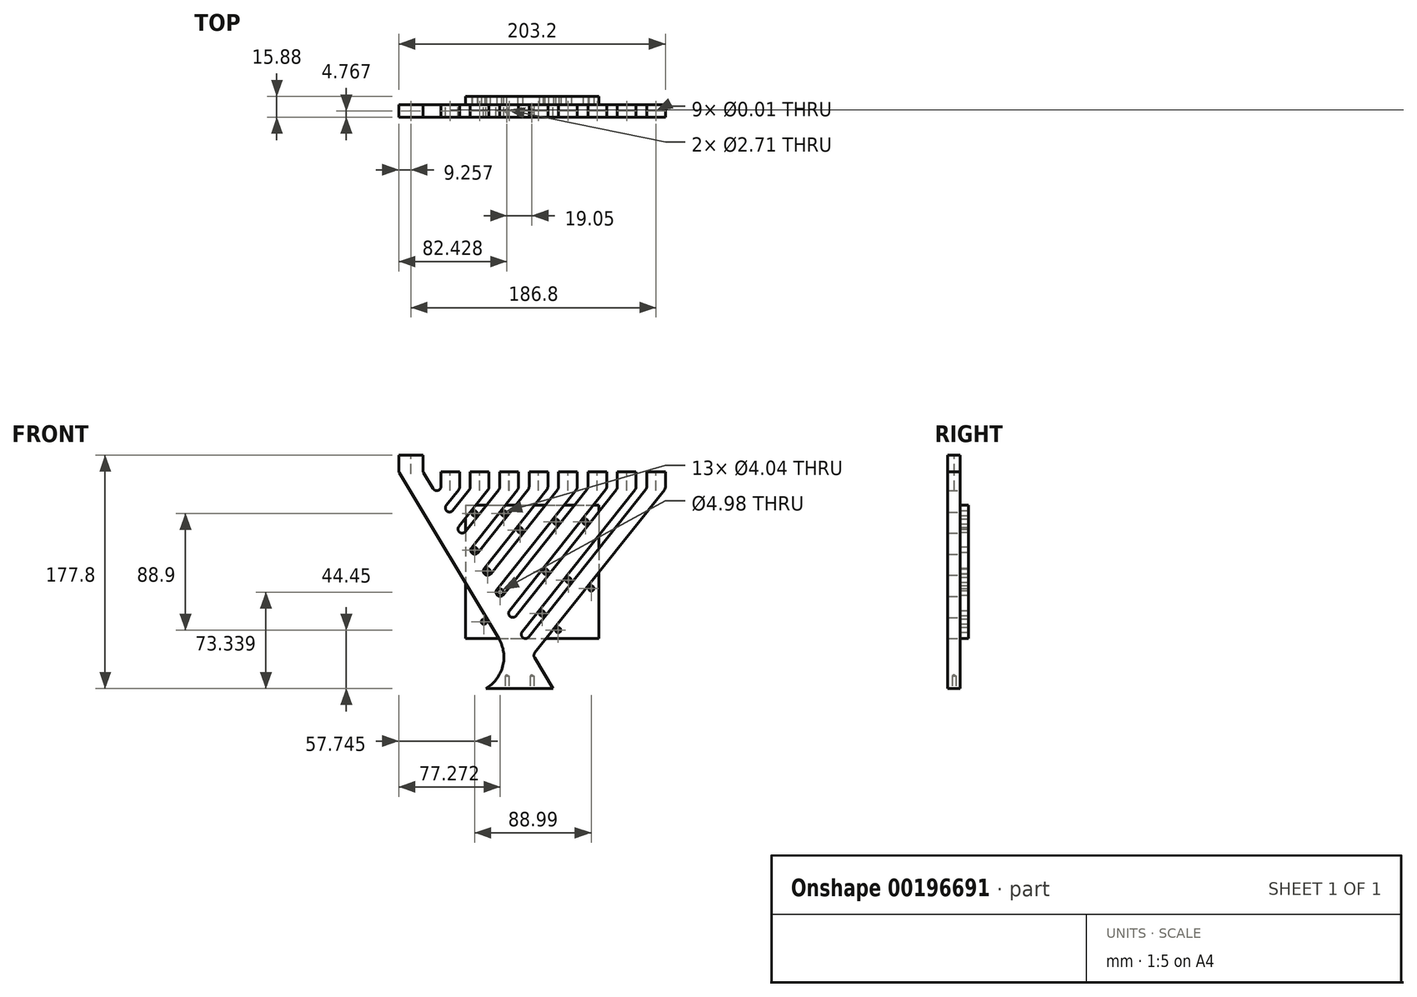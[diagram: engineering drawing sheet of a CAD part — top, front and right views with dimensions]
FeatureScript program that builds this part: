
annotation { "Feature Type Name" : "Feature", "Feature Type Description" : "" }
export const myFeature = defineFeature(function(context is Context, id is Id, definition is map)
    precondition{}
    {
        {
            var Q0;
            Q0=qCreatedBy(makeId("Front.planeOp"),FACE);
            var sketch = newSketch(context, id + "F0", { "sketchPlane" : qUnion([Q0])});
            skLineSegment(sketch, "E0", {"start": v(0, -12.7) * mm, "end": v(76.2, -139.7) * mm});
            skLineSegment(sketch, "E1", {"start": v(66.33, -177.8) * mm, "end": v(117.57, -177.8) * mm});
            skLineSegment(sketch, "E2", {"start": v(117.57, -177.8) * mm, "end": v(102.33, -152.4) * mm});
            skLineSegment(sketch, "E3", {"start": v(102.33, -152.4) * mm, "end": v(203.2, -25.4) * mm});
            skArc(sketch, "E4", {"start": v(76.2, -139.7) * mm, "mid": v(79.25, -160.82) * mm, "end": v(66.33, -177.8) * mm});
            skLineSegment(sketch, "E5.1.0.0", {"start": v(92.7, -136.34) * mm, "end": v(193.56, -9.34) * mm});
            skLineSegment(sketch, "E5.2.0.0", {"start": v(83.06, -120.27) * mm, "end": v(183.92, 6.73) * mm});
            skLineSegment(sketch, "E5.direction1", {"start": v(102.33, -152.4) * mm, "end": v(92.7, -136.34) * mm, "construction": true});
            skLineSegment(sketch, "E6.0.3.0", {"start": v(73.42, -104.2) * mm, "end": v(174.29, 22.8) * mm});
            skLineSegment(sketch, "E6.0.4.0", {"start": v(63.78, -88.14) * mm, "end": v(164.65, 38.86) * mm});
            skLineSegment(sketch, "E6.0.5.0", {"start": v(54.14, -72.08) * mm, "end": v(155, 54.92) * mm});
            skLineSegment(sketch, "E6.0.6.0", {"start": v(44.5, -56.02) * mm, "end": v(145.37, 70.98) * mm});
            skLineSegment(sketch, "E6.0.7.0", {"start": v(34.87, -39.95) * mm, "end": v(135.73, 87.05) * mm});
            skLineSegment(sketch, "E7", {"start": v(96.18, -142.15) * mm, "end": v(197.05, -15.15) * mm});
            skLineSegment(sketch, "E8.1.0.0", {"start": v(86.55, -126.09) * mm, "end": v(187.41, 0.91) * mm});
            skLineSegment(sketch, "E8.2.0.0", {"start": v(76.9, -110.02) * mm, "end": v(177.77, 16.98) * mm});
            skLineSegment(sketch, "E8.direction1", {"start": v(96.18, -142.15) * mm, "end": v(86.55, -126.09) * mm, "construction": true});
            skLineSegment(sketch, "E9.0.3.0", {"start": v(67.27, -93.96) * mm, "end": v(168.14, 33.04) * mm});
            skLineSegment(sketch, "E9.0.4.0", {"start": v(57.63, -77.9) * mm, "end": v(158.5, 49.1) * mm});
            skLineSegment(sketch, "E9.0.5.0", {"start": v(48, -61.83) * mm, "end": v(148.86, 65.17) * mm});
            skLineSegment(sketch, "E9.0.6.0", {"start": v(38.35, -45.77) * mm, "end": v(139.22, 81.23) * mm});
            skLineSegment(sketch, "E9.0.7.0", {"start": v(28.72, -29.7) * mm, "end": v(129.58, 97.3) * mm});
            skLineSegment(sketch, "E10", {"start": v(203.2, -25.4) * mm, "end": v(-58.22, -25.4) * mm});
            skLineSegment(sketch, "E11", {"start": v(102.33, -152.4) * mm, "end": v(28.72, -29.7) * mm});
            skLineSegment(sketch, "E12", {"start": v(28.72, -29.7) * mm, "end": v(18.51, -12.7) * mm});
            skLineSegment(sketch, "E13", {"start": v(18.51, -12.7) * mm, "end": v(0, -12.7) * mm});
            skPoint(sketch, "E14", {"position": v(180.8, -25.4) * mm});
            skLineSegment(sketch, "E15", {"start": v(66.33, -177.8) * mm, "end": v(34.1, -196.4) * mm, "construction": true});
            skLineSegment(sketch, "E16", {"start": v(0, -12.7) * mm, "end": v(0, 0) * mm});
            skLineSegment(sketch, "E17", {"start": v(18.51, -12.7) * mm, "end": v(203.2, -12.7) * mm, "construction": true});
            skPoint(sketch, "E18", {"position": v(32.14, -25.4) * mm});
            skPoint(sketch, "E19", {"position": v(46.42, -25.4) * mm});
            skPoint(sketch, "E20", {"position": v(54.53, -25.4) * mm});
            skPoint(sketch, "E21", {"position": v(68.82, -25.4) * mm});
            skPoint(sketch, "E22", {"position": v(76.93, -25.4) * mm});
            skPoint(sketch, "E23", {"position": v(91.22, -25.4) * mm});
            skPoint(sketch, "E24", {"position": v(99.33, -25.4) * mm});
            skPoint(sketch, "E25", {"position": v(114.21, -24.64) * mm});
            skPoint(sketch, "E26", {"position": v(121.72, -25.4) * mm});
            skPoint(sketch, "E27", {"position": v(136.01, -25.4) * mm});
            skPoint(sketch, "E28", {"position": v(144.12, -25.4) * mm});
            skPoint(sketch, "E29", {"position": v(158.4, -25.4) * mm});
            skPoint(sketch, "E30", {"position": v(166.52, -25.4) * mm});
            skPoint(sketch, "E31", {"position": v(188.91, -25.4) * mm});
            skLineSegment(sketch, "E32", {"start": v(117.57, -177.8) * mm, "end": v(125.2, -190.5) * mm});
            skSolve(sketch);
        }
        {
            var Q0;
            Q0=makeQuery(id+"F0.imprint","IMPRINT",FACE,{"disambiguationData":[TD([[makeQuery(id+"F0.imprint","IMPRINT",EDGE,{"derivedFrom":sQuery(id+"F0.wireOp",EDGE,"E1")}),1.0]])]});
            var Q1;
            {var subQ0=sQuery(id+"F0.wireOp",EDGE,"E13");Q1=makeQuery(id+"F0.imprint","IMPRINT",FACE,{"disambiguationData":[TD([[makeQuery(id+"F0.imprint","IMPRINT",EDGE,{"derivedFrom":subQ0}),1.0]])]});}
            var Q2;
            {var subQ0=sQuery(id+"F0.wireOp",EDGE,"E11");var subQ1=sQuery(id+"F0.wireOp",EDGE,"E6.0.7.0");var subQ2=makeQuery(id+"F0.imprint","INTERSECT",VERTEX,{"derivedFrom":[subQ1,subQ0]});Q2=makeQuery(id+"F0.imprint","IMPRINT",FACE,{"disambiguationData":[TD([[makeQuery(id+"F0.imprint","IMPRINT",EDGE,{"disambiguationData":[TD([[subQ2,-1.0]])],"derivedFrom":subQ1}),1.0]])]});}
            var Q3;
            {var subQ0=sQuery(id+"F0.wireOp",EDGE,"E11");var subQ1=sQuery(id+"F0.wireOp",EDGE,"E6.0.6.0");var subQ2=makeQuery(id+"F0.imprint","INTERSECT",VERTEX,{"derivedFrom":[subQ1,subQ0]});Q3=makeQuery(id+"F0.imprint","IMPRINT",FACE,{"disambiguationData":[TD([[makeQuery(id+"F0.imprint","IMPRINT",EDGE,{"disambiguationData":[TD([[subQ2,-1.0]])],"derivedFrom":subQ1}),1.0]])]});}
            var Q4;
            {var subQ0=sQuery(id+"F0.wireOp",EDGE,"E11");var subQ1=sQuery(id+"F0.wireOp",EDGE,"E6.0.5.0");var subQ2=makeQuery(id+"F0.imprint","INTERSECT",VERTEX,{"derivedFrom":[subQ1,subQ0]});Q4=makeQuery(id+"F0.imprint","IMPRINT",FACE,{"disambiguationData":[TD([[makeQuery(id+"F0.imprint","IMPRINT",EDGE,{"disambiguationData":[TD([[subQ2,-1.0]])],"derivedFrom":subQ1}),1.0]])]});}
            var Q5;
            {var subQ0=sQuery(id+"F0.wireOp",EDGE,"E11");var subQ1=sQuery(id+"F0.wireOp",EDGE,"E6.0.4.0");var subQ2=makeQuery(id+"F0.imprint","INTERSECT",VERTEX,{"derivedFrom":[subQ1,subQ0]});Q5=makeQuery(id+"F0.imprint","IMPRINT",FACE,{"disambiguationData":[TD([[makeQuery(id+"F0.imprint","IMPRINT",EDGE,{"disambiguationData":[TD([[subQ2,-1.0]])],"derivedFrom":subQ1}),1.0]])]});}
            var Q6;
            {var subQ0=sQuery(id+"F0.wireOp",EDGE,"E11");var subQ1=sQuery(id+"F0.wireOp",EDGE,"E6.0.3.0");var subQ2=makeQuery(id+"F0.imprint","INTERSECT",VERTEX,{"derivedFrom":[subQ1,subQ0]});Q6=makeQuery(id+"F0.imprint","IMPRINT",FACE,{"disambiguationData":[TD([[makeQuery(id+"F0.imprint","IMPRINT",EDGE,{"disambiguationData":[TD([[subQ2,-1.0]])],"derivedFrom":subQ1}),1.0]])]});}
            var Q7;
            {var subQ0=sQuery(id+"F0.wireOp",EDGE,"E11");var subQ1=sQuery(id+"F0.wireOp",EDGE,"E5.2.0.0");var subQ2=makeQuery(id+"F0.imprint","INTERSECT",VERTEX,{"derivedFrom":[subQ1,subQ0]});Q7=makeQuery(id+"F0.imprint","IMPRINT",FACE,{"disambiguationData":[TD([[makeQuery(id+"F0.imprint","IMPRINT",EDGE,{"disambiguationData":[TD([[subQ2,-1.0]])],"derivedFrom":subQ1}),1.0]])]});}
            var Q8;
            {var subQ0=sQuery(id+"F0.wireOp",EDGE,"E11");var subQ1=sQuery(id+"F0.wireOp",EDGE,"E5.1.0.0");var subQ2=makeQuery(id+"F0.imprint","INTERSECT",VERTEX,{"derivedFrom":[subQ1,subQ0]});Q8=makeQuery(id+"F0.imprint","IMPRINT",FACE,{"disambiguationData":[TD([[makeQuery(id+"F0.imprint","IMPRINT",EDGE,{"disambiguationData":[TD([[subQ2,-1.0]])],"derivedFrom":subQ1}),1.0]])]});}
            var Q9;
            {var subQ0=sQuery(id+"F0.wireOp",EDGE,"E3");Q9=makeQuery(id+"F0.imprint","IMPRINT",FACE,{"disambiguationData":[TD([[makeQuery(id+"F0.imprint","IMPRINT",EDGE,{"derivedFrom":subQ0}),1.0]])]});}
            extrude(context, id + "F1", {"entities" : qUnion([Q0, Q1, Q2, Q3, Q4, Q5, Q6, Q7, Q8, Q9]), "flatOperationType" : FlatOperationType.REMOVE, "offsetDistance" : 25.4 * mm, "depth" : 9.52 * mm, "domain" : OperationDomain.MODEL});
        }
        {
            var Q0;
            Q0=makeQuery(id+"F1.opExtrude","SWEPT_EDGE",EDGE,{"disambiguationData":[OSD([sQuery(id+"F0.wireOp",EDGE,"E9.0.6.0"),sQuery(id+"F0.wireOp",EDGE,"E11")])]});
            var Q1;
            Q1=makeQuery(id+"F1.opExtrude","SWEPT_EDGE",EDGE,{"disambiguationData":[OSD([sQuery(id+"F0.wireOp",EDGE,"E9.0.5.0"),sQuery(id+"F0.wireOp",EDGE,"E11")])]});
            var Q2;
            Q2=makeQuery(id+"F1.opExtrude","SWEPT_EDGE",EDGE,{"disambiguationData":[OSD([sQuery(id+"F0.wireOp",EDGE,"E9.0.4.0"),sQuery(id+"F0.wireOp",EDGE,"E11")])]});
            var Q3;
            Q3=makeQuery(id+"F1.opExtrude","SWEPT_EDGE",EDGE,{"disambiguationData":[OSD([sQuery(id+"F0.wireOp",EDGE,"E9.0.3.0"),sQuery(id+"F0.wireOp",EDGE,"E11")])]});
            var Q4;
            Q4=makeQuery(id+"F1.opExtrude","SWEPT_EDGE",EDGE,{"disambiguationData":[OSD([sQuery(id+"F0.wireOp",EDGE,"E8.2.0.0"),sQuery(id+"F0.wireOp",EDGE,"E11")])]});
            var Q5;
            Q5=makeQuery(id+"F1.opExtrude","SWEPT_EDGE",EDGE,{"disambiguationData":[OSD([sQuery(id+"F0.wireOp",EDGE,"E8.1.0.0"),sQuery(id+"F0.wireOp",EDGE,"E11")])]});
            var Q6;
            Q6=makeQuery(id+"F1.opExtrude","SWEPT_EDGE",EDGE,{"disambiguationData":[OSD([sQuery(id+"F0.wireOp",EDGE,"E7"),sQuery(id+"F0.wireOp",EDGE,"E11")])]});
            fillet(context, id + "F2", {"entities" : qUnion([Q0, Q1, Q2, Q3, Q4, Q5, Q6]), "radius" : 3.17 * mm, "tangentPropagation" : true, "allowEdgeOverflow" : false});
        }
        {
            var Q0;
            Q0=makeQuery(id+"F1.opExtrude","SWEPT_EDGE",EDGE,{"disambiguationData":[OSD([sQuery(id+"F0.wireOp",EDGE,"E6.0.7.0"),sQuery(id+"F0.wireOp",EDGE,"E11")])]});
            var Q1;
            Q1=makeQuery(id+"F1.opExtrude","SWEPT_EDGE",EDGE,{"disambiguationData":[OSD([sQuery(id+"F0.wireOp",EDGE,"E6.0.6.0"),sQuery(id+"F0.wireOp",EDGE,"E11")])]});
            var Q2;
            Q2=makeQuery(id+"F1.opExtrude","SWEPT_EDGE",EDGE,{"disambiguationData":[OSD([sQuery(id+"F0.wireOp",EDGE,"E6.0.5.0"),sQuery(id+"F0.wireOp",EDGE,"E11")])]});
            var Q3;
            Q3=makeQuery(id+"F1.opExtrude","SWEPT_EDGE",EDGE,{"disambiguationData":[OSD([sQuery(id+"F0.wireOp",EDGE,"E6.0.4.0"),sQuery(id+"F0.wireOp",EDGE,"E11")])]});
            var Q4;
            Q4=makeQuery(id+"F1.opExtrude","SWEPT_EDGE",EDGE,{"disambiguationData":[OSD([sQuery(id+"F0.wireOp",EDGE,"E6.0.3.0"),sQuery(id+"F0.wireOp",EDGE,"E11")])]});
            var Q5;
            Q5=makeQuery(id+"F1.opExtrude","SWEPT_EDGE",EDGE,{"disambiguationData":[OSD([sQuery(id+"F0.wireOp",EDGE,"E5.2.0.0"),sQuery(id+"F0.wireOp",EDGE,"E11")])]});
            var Q6;
            Q6=makeQuery(id+"F1.opExtrude","SWEPT_EDGE",EDGE,{"disambiguationData":[OSD([sQuery(id+"F0.wireOp",EDGE,"E5.1.0.0"),sQuery(id+"F0.wireOp",EDGE,"E11")])]});
            var Q7;
            Q7=makeQuery(id+"F1.opExtrude","SWEPT_EDGE",EDGE,{"disambiguationData":[OSD([sQuery(id+"F0.wireOp",EDGE,"E2"),sQuery(id+"F0.wireOp",EDGE,"E3"),sQuery(id+"F0.wireOp",EDGE,"E11")])]});
            fillet(context, id + "F3", {"entities" : qUnion([Q0, Q1, Q2, Q3, Q4, Q5, Q6, Q7]), "radius" : 3.17 * mm, "tangentPropagation" : true, "allowEdgeOverflow" : false});
        }
        {
            var Q0;
            Q0=makeQuery(id+"F1.opExtrude","SWEPT_FACE",FACE,{"disambiguationData":[OSD([sQuery(id+"F0.wireOp",EDGE,"E13")])]});
            extrude(context, id + "F4", {"entities" : qUnion([Q0]), "operationType" : NewBodyOperationType.ADD, "depth" : 12.7 * mm});
        }
        {
            var Q0;
            {var subQ0=sQuery(id+"F0.wireOp",EDGE,"E10");Q0=makeQuery(id+"F1.opExtrude","SWEPT_FACE",FACE,{"disambiguationData":[OSD([subQ0]),TDD([makeQuery(id+"F0.imprint","IMPRINT",EDGE,{"disambiguationData":[TD([[makeQuery(id+"F0.imprint","INTERSECT",VERTEX,{"derivedFrom":[sQuery(id+"F0.wireOp",EDGE,"E6.0.7.0"),subQ0]}),-1.0]])],"derivedFrom":subQ0})])]});}
            var Q1;
            {var subQ0=sQuery(id+"F0.wireOp",EDGE,"E10");Q1=makeQuery(id+"F1.opExtrude","SWEPT_FACE",FACE,{"disambiguationData":[OSD([subQ0]),TDD([makeQuery(id+"F0.imprint","IMPRINT",EDGE,{"disambiguationData":[TD([[makeQuery(id+"F0.imprint","INTERSECT",VERTEX,{"derivedFrom":[sQuery(id+"F0.wireOp",EDGE,"E6.0.6.0"),subQ0]}),-1.0]])],"derivedFrom":subQ0})])]});}
            var Q2;
            {var subQ0=sQuery(id+"F0.wireOp",EDGE,"E10");Q2=makeQuery(id+"F1.opExtrude","SWEPT_FACE",FACE,{"disambiguationData":[OSD([subQ0]),TDD([makeQuery(id+"F0.imprint","IMPRINT",EDGE,{"disambiguationData":[TD([[makeQuery(id+"F0.imprint","INTERSECT",VERTEX,{"derivedFrom":[sQuery(id+"F0.wireOp",EDGE,"E6.0.5.0"),subQ0]}),-1.0]])],"derivedFrom":subQ0})])]});}
            var Q3;
            {var subQ0=sQuery(id+"F0.wireOp",EDGE,"E10");Q3=makeQuery(id+"F1.opExtrude","SWEPT_FACE",FACE,{"disambiguationData":[OSD([subQ0]),TDD([makeQuery(id+"F0.imprint","IMPRINT",EDGE,{"disambiguationData":[TD([[makeQuery(id+"F0.imprint","INTERSECT",VERTEX,{"derivedFrom":[sQuery(id+"F0.wireOp",EDGE,"E6.0.4.0"),subQ0]}),-1.0]])],"derivedFrom":subQ0})])]});}
            var Q4;
            {var subQ0=sQuery(id+"F0.wireOp",EDGE,"E10");Q4=makeQuery(id+"F1.opExtrude","SWEPT_FACE",FACE,{"disambiguationData":[OSD([subQ0]),TDD([makeQuery(id+"F0.imprint","IMPRINT",EDGE,{"disambiguationData":[TD([[makeQuery(id+"F0.imprint","INTERSECT",VERTEX,{"derivedFrom":[sQuery(id+"F0.wireOp",EDGE,"E6.0.3.0"),subQ0]}),-1.0]])],"derivedFrom":subQ0})])]});}
            var Q5;
            {var subQ0=sQuery(id+"F0.wireOp",EDGE,"E10");Q5=makeQuery(id+"F1.opExtrude","SWEPT_FACE",FACE,{"disambiguationData":[OSD([subQ0]),TDD([makeQuery(id+"F0.imprint","IMPRINT",EDGE,{"disambiguationData":[TD([[makeQuery(id+"F0.imprint","INTERSECT",VERTEX,{"derivedFrom":[sQuery(id+"F0.wireOp",EDGE,"E5.2.0.0"),subQ0]}),-1.0]])],"derivedFrom":subQ0})])]});}
            var Q6;
            {var subQ0=sQuery(id+"F0.wireOp",EDGE,"E10");Q6=makeQuery(id+"F1.opExtrude","SWEPT_FACE",FACE,{"disambiguationData":[OSD([subQ0]),TDD([makeQuery(id+"F0.imprint","IMPRINT",EDGE,{"disambiguationData":[TD([[makeQuery(id+"F0.imprint","INTERSECT",VERTEX,{"derivedFrom":[sQuery(id+"F0.wireOp",EDGE,"E5.1.0.0"),subQ0]}),-1.0]])],"derivedFrom":subQ0})])]});}
            var Q7;
            {var subQ0=sQuery(id+"F0.wireOp",EDGE,"E10");Q7=makeQuery(id+"F1.opExtrude","SWEPT_FACE",FACE,{"disambiguationData":[OSD([subQ0]),TDD([makeQuery(id+"F0.imprint","IMPRINT",EDGE,{"disambiguationData":[TD([[makeQuery(id+"F0.imprint","INTERSECT",VERTEX,{"derivedFrom":[sQuery(id+"F0.wireOp",EDGE,"E3"),subQ0]}),-1.0]])],"derivedFrom":subQ0})])]});}
            extrude(context, id + "F5", {"entities" : qUnion([Q0, Q1, Q2, Q3, Q4, Q5, Q6, Q7]), "operationType" : NewBodyOperationType.ADD, "depth" : 12.7 * mm});
        }
        {
            var Q0;
            {var subQ0=sQuery(id+"F0.wireOp",EDGE,"E10");var subQ1=sQuery(id+"F0.wireOp",EDGE,"E9.0.6.0");Q0=makeQuery(id+"F5.boolean.opBoolean","MERGE",EDGE,{"derivedFrom":[makeQuery(id+"F1.opExtrude","SWEPT_EDGE",EDGE,{"disambiguationData":[OSD([subQ1,subQ0])]}),makeQuery(id+"F5.opExtrude","CAP_EDGE",EDGE,{"disambiguationData":[OSD([subQ1,subQ0])],"isStart":true})]});}
            var Q1;
            {var subQ0=sQuery(id+"F0.wireOp",EDGE,"E10");var subQ1=sQuery(id+"F0.wireOp",EDGE,"E9.0.5.0");Q1=makeQuery(id+"F5.boolean.opBoolean","MERGE",EDGE,{"derivedFrom":[makeQuery(id+"F1.opExtrude","SWEPT_EDGE",EDGE,{"disambiguationData":[OSD([subQ1,subQ0])]}),makeQuery(id+"F5.opExtrude","CAP_EDGE",EDGE,{"disambiguationData":[OSD([subQ1,subQ0])],"isStart":true})]});}
            var Q2;
            {var subQ0=sQuery(id+"F0.wireOp",EDGE,"E10");var subQ1=sQuery(id+"F0.wireOp",EDGE,"E9.0.4.0");Q2=makeQuery(id+"F5.boolean.opBoolean","MERGE",EDGE,{"derivedFrom":[makeQuery(id+"F1.opExtrude","SWEPT_EDGE",EDGE,{"disambiguationData":[OSD([subQ1,subQ0])]}),makeQuery(id+"F5.opExtrude","CAP_EDGE",EDGE,{"disambiguationData":[OSD([subQ1,subQ0])],"isStart":true})]});}
            var Q3;
            {var subQ0=sQuery(id+"F0.wireOp",EDGE,"E10");var subQ1=sQuery(id+"F0.wireOp",EDGE,"E9.0.3.0");Q3=makeQuery(id+"F5.boolean.opBoolean","MERGE",EDGE,{"derivedFrom":[makeQuery(id+"F1.opExtrude","SWEPT_EDGE",EDGE,{"disambiguationData":[OSD([subQ1,subQ0])]}),makeQuery(id+"F5.opExtrude","CAP_EDGE",EDGE,{"disambiguationData":[OSD([subQ1,subQ0])],"isStart":true})]});}
            var Q4;
            {var subQ0=sQuery(id+"F0.wireOp",EDGE,"E10");var subQ1=sQuery(id+"F0.wireOp",EDGE,"E8.2.0.0");Q4=makeQuery(id+"F5.boolean.opBoolean","MERGE",EDGE,{"derivedFrom":[makeQuery(id+"F1.opExtrude","SWEPT_EDGE",EDGE,{"disambiguationData":[OSD([subQ1,subQ0])]}),makeQuery(id+"F5.opExtrude","CAP_EDGE",EDGE,{"disambiguationData":[OSD([subQ1,subQ0])],"isStart":true})]});}
            var Q5;
            {var subQ0=sQuery(id+"F0.wireOp",EDGE,"E10");var subQ1=sQuery(id+"F0.wireOp",EDGE,"E8.1.0.0");Q5=makeQuery(id+"F5.boolean.opBoolean","MERGE",EDGE,{"derivedFrom":[makeQuery(id+"F1.opExtrude","SWEPT_EDGE",EDGE,{"disambiguationData":[OSD([subQ1,subQ0])]}),makeQuery(id+"F5.opExtrude","CAP_EDGE",EDGE,{"disambiguationData":[OSD([subQ1,subQ0])],"isStart":true})]});}
            var Q6;
            {var subQ0=sQuery(id+"F0.wireOp",EDGE,"E10");var subQ1=sQuery(id+"F0.wireOp",EDGE,"E7");Q6=makeQuery(id+"F5.boolean.opBoolean","MERGE",EDGE,{"derivedFrom":[makeQuery(id+"F1.opExtrude","SWEPT_EDGE",EDGE,{"disambiguationData":[OSD([subQ1,subQ0])]}),makeQuery(id+"F5.opExtrude","CAP_EDGE",EDGE,{"disambiguationData":[OSD([subQ1,subQ0])],"isStart":true})]});}
            var Q7;
            {var subQ0=sQuery(id+"F0.wireOp",EDGE,"E13");var subQ1=sQuery(id+"F0.wireOp",EDGE,"E12");Q7=makeQuery(id+"F4.boolean.opBoolean","MERGE",EDGE,{"derivedFrom":[makeQuery(id+"F1.opExtrude","SWEPT_EDGE",EDGE,{"disambiguationData":[OSD([subQ1,subQ0])]}),makeQuery(id+"F4.opExtrude","CAP_EDGE",EDGE,{"disambiguationData":[OSD([subQ1,subQ0])],"isStart":true})]});}
            fillet(context, id + "F6", {"entities" : qUnion([Q0, Q1, Q2, Q3, Q4, Q5, Q6, Q7]), "radius" : 3.17 * mm, "tangentPropagation" : true, "allowEdgeOverflow" : false});
        }
        {
            var Q0;
            {var subQ0=sQuery(id+"F0.wireOp",EDGE,"E10");var subQ1=sQuery(id+"F0.wireOp",EDGE,"E6.0.7.0");Q0=makeQuery(id+"F5.boolean.opBoolean","MERGE",EDGE,{"derivedFrom":[makeQuery(id+"F1.opExtrude","SWEPT_EDGE",EDGE,{"disambiguationData":[OSD([subQ1,subQ0])]}),makeQuery(id+"F5.opExtrude","CAP_EDGE",EDGE,{"disambiguationData":[OSD([subQ1,subQ0])],"isStart":true})]});}
            var Q1;
            {var subQ0=sQuery(id+"F0.wireOp",EDGE,"E10");var subQ1=sQuery(id+"F0.wireOp",EDGE,"E6.0.6.0");Q1=makeQuery(id+"F5.boolean.opBoolean","MERGE",EDGE,{"derivedFrom":[makeQuery(id+"F1.opExtrude","SWEPT_EDGE",EDGE,{"disambiguationData":[OSD([subQ1,subQ0])]}),makeQuery(id+"F5.opExtrude","CAP_EDGE",EDGE,{"disambiguationData":[OSD([subQ1,subQ0])],"isStart":true})]});}
            var Q2;
            {var subQ0=sQuery(id+"F0.wireOp",EDGE,"E10");var subQ1=sQuery(id+"F0.wireOp",EDGE,"E6.0.5.0");Q2=makeQuery(id+"F5.boolean.opBoolean","MERGE",EDGE,{"derivedFrom":[makeQuery(id+"F1.opExtrude","SWEPT_EDGE",EDGE,{"disambiguationData":[OSD([subQ1,subQ0])]}),makeQuery(id+"F5.opExtrude","CAP_EDGE",EDGE,{"disambiguationData":[OSD([subQ1,subQ0])],"isStart":true})]});}
            var Q3;
            {var subQ0=sQuery(id+"F0.wireOp",EDGE,"E10");var subQ1=sQuery(id+"F0.wireOp",EDGE,"E6.0.4.0");Q3=makeQuery(id+"F5.boolean.opBoolean","MERGE",EDGE,{"derivedFrom":[makeQuery(id+"F1.opExtrude","SWEPT_EDGE",EDGE,{"disambiguationData":[OSD([subQ1,subQ0])]}),makeQuery(id+"F5.opExtrude","CAP_EDGE",EDGE,{"disambiguationData":[OSD([subQ1,subQ0])],"isStart":true})]});}
            var Q4;
            {var subQ0=sQuery(id+"F0.wireOp",EDGE,"E10");var subQ1=sQuery(id+"F0.wireOp",EDGE,"E6.0.3.0");Q4=makeQuery(id+"F5.boolean.opBoolean","MERGE",EDGE,{"derivedFrom":[makeQuery(id+"F1.opExtrude","SWEPT_EDGE",EDGE,{"disambiguationData":[OSD([subQ1,subQ0])]}),makeQuery(id+"F5.opExtrude","CAP_EDGE",EDGE,{"disambiguationData":[OSD([subQ1,subQ0])],"isStart":true})]});}
            var Q5;
            {var subQ0=sQuery(id+"F0.wireOp",EDGE,"E10");var subQ1=sQuery(id+"F0.wireOp",EDGE,"E5.2.0.0");Q5=makeQuery(id+"F5.boolean.opBoolean","MERGE",EDGE,{"derivedFrom":[makeQuery(id+"F1.opExtrude","SWEPT_EDGE",EDGE,{"disambiguationData":[OSD([subQ1,subQ0])]}),makeQuery(id+"F5.opExtrude","CAP_EDGE",EDGE,{"disambiguationData":[OSD([subQ1,subQ0])],"isStart":true})]});}
            var Q6;
            {var subQ0=sQuery(id+"F0.wireOp",EDGE,"E10");var subQ1=sQuery(id+"F0.wireOp",EDGE,"E5.1.0.0");Q6=makeQuery(id+"F5.boolean.opBoolean","MERGE",EDGE,{"derivedFrom":[makeQuery(id+"F1.opExtrude","SWEPT_EDGE",EDGE,{"disambiguationData":[OSD([subQ1,subQ0])]}),makeQuery(id+"F5.opExtrude","CAP_EDGE",EDGE,{"disambiguationData":[OSD([subQ1,subQ0])],"isStart":true})]});}
            var Q7;
            {var subQ0=sQuery(id+"F0.wireOp",EDGE,"E10");var subQ1=sQuery(id+"F0.wireOp",EDGE,"E3");Q7=makeQuery(id+"F5.boolean.opBoolean","MERGE",EDGE,{"derivedFrom":[makeQuery(id+"F1.opExtrude","SWEPT_EDGE",EDGE,{"disambiguationData":[OSD([subQ1,subQ0])]}),makeQuery(id+"F5.opExtrude","CAP_EDGE",EDGE,{"disambiguationData":[OSD([subQ1,subQ0])],"isStart":true})]});}
            var Q8;
            {var subQ0=sQuery(id+"F0.wireOp",EDGE,"E13");var subQ1=sQuery(id+"F0.wireOp",EDGE,"E0");Q8=makeQuery(id+"F4.boolean.opBoolean","MERGE",EDGE,{"derivedFrom":[makeQuery(id+"F1.opExtrude","SWEPT_EDGE",EDGE,{"disambiguationData":[OSD([subQ1,subQ0])]}),makeQuery(id+"F4.opExtrude","CAP_EDGE",EDGE,{"disambiguationData":[OSD([subQ1,subQ0])],"isStart":true})]});}
            fillet(context, id + "F7", {"entities" : qUnion([Q0, Q1, Q2, Q3, Q4, Q5, Q6, Q7, Q8]), "radius" : 3.17 * mm, "tangentPropagation" : true, "allowEdgeOverflow" : false});
        }
        {
            var Q0;
            Q0=qCreatedBy(makeId("Front.planeOp"),FACE);
            var sketch = newSketch(context, id + "F8", { "sketchPlane" : qUnion([Q0])});
            skCircle(sketch, "E33", {"center": v(28.96, -23.94) * mm, "radius": 3.18 * mm});
            skLineSegment(sketch, "E34", {"start": v(32.14, -23.94) * mm, "end": v(32.14, -25.4) * mm});
            skLineSegment(sketch, "E35", {"start": v(32.14, -25.4) * mm, "end": v(28.72, -29.7) * mm});
            skLineSegment(sketch, "E36", {"start": v(28.72, -29.7) * mm, "end": v(26.24, -25.58) * mm});
            skSolve(sketch);
        }
        {
            var Q0;
            {var subQ0=sQuery(id+"F8.wireOp",EDGE,"E34");Q0=makeQuery(id+"F8.imprint","IMPRINT",FACE,{"disambiguationData":[TD([[makeQuery(id+"F8.imprint","IMPRINT",EDGE,{"derivedFrom":subQ0}),-1.0]])]});}
            var Q1;
            {var subQ0=sQuery(id+"F0.wireOp",EDGE,"E10");var subQ1=sQuery(id+"F0.wireOp",EDGE,"E6.0.7.0");var subQ2=sQuery(id+"F0.wireOp",EDGE,"E9.0.7.0");var subQ3=sQuery(id+"F0.wireOp",EDGE,"E6.0.6.0");var subQ4=sQuery(id+"F0.wireOp",EDGE,"E9.0.6.0");var subQ5=sQuery(id+"F0.wireOp",EDGE,"E6.0.5.0");var subQ6=sQuery(id+"F0.wireOp",EDGE,"E9.0.5.0");var subQ7=sQuery(id+"F0.wireOp",EDGE,"E6.0.4.0");var subQ8=sQuery(id+"F0.wireOp",EDGE,"E9.0.4.0");var subQ9=sQuery(id+"F0.wireOp",EDGE,"E6.0.3.0");var subQ10=sQuery(id+"F0.wireOp",EDGE,"E9.0.3.0");var subQ11=sQuery(id+"F0.wireOp",EDGE,"E5.2.0.0");var subQ12=sQuery(id+"F0.wireOp",EDGE,"E8.2.0.0");var subQ13=sQuery(id+"F0.wireOp",EDGE,"E5.1.0.0");var subQ14=sQuery(id+"F0.wireOp",EDGE,"E8.1.0.0");var subQ15=sQuery(id+"F0.wireOp",EDGE,"E3");var subQ16=sQuery(id+"F0.wireOp",EDGE,"E7");var subQ17=sQuery(id+"F0.wireOp",EDGE,"E13");Q1=makeQuery(id+"F5.boolean.opBoolean","MERGE",FACE,{"derivedFrom":[makeQuery(id+"F4.boolean.opBoolean","MERGE",FACE,{"derivedFrom":[makeQuery(id+"F1.opExtrude","CAP_FACE",FACE,{"disambiguationData":[OSD([sQuery(id+"F0.wireOp",EDGE,"E0"),sQuery(id+"F0.wireOp",EDGE,"E1"),sQuery(id+"F0.wireOp",EDGE,"E2"),subQ15,sQuery(id+"F0.wireOp",EDGE,"E4"),subQ13,subQ11,subQ9,subQ7,subQ5,subQ3,subQ1,subQ16,subQ14,subQ12,subQ10,subQ8,subQ6,subQ4,subQ2,subQ0,sQuery(id+"F0.wireOp",EDGE,"E11"),sQuery(id+"F0.wireOp",EDGE,"E12"),subQ17])],"isStart":false}),makeQuery(id+"F4.opExtrude","SWEPT_FACE",FACE,{"disambiguationData":[OSD([subQ17]),TDD([makeQuery(id+"F1.opExtrude","CAP_EDGE",EDGE,{"disambiguationData":[OSD([subQ17])],"isStart":false})])]})]}),makeQuery(id+"F5.opExtrude","SWEPT_FACE",FACE,{"disambiguationData":[OSD([subQ0]),TDD([makeQuery(id+"F1.opExtrude","CAP_EDGE",EDGE,{"disambiguationData":[OSD([subQ0]),TDD([makeQuery(id+"F0.imprint","IMPRINT",EDGE,{"disambiguationData":[TD([[makeQuery(id+"F0.imprint","INTERSECT",VERTEX,{"derivedFrom":[subQ15,subQ0]}),-1.0]])],"derivedFrom":subQ0})])],"isStart":false})])]}),makeQuery(id+"F5.opExtrude","SWEPT_FACE",FACE,{"disambiguationData":[OSD([subQ0]),TDD([makeQuery(id+"F1.opExtrude","CAP_EDGE",EDGE,{"disambiguationData":[OSD([subQ0]),TDD([makeQuery(id+"F0.imprint","IMPRINT",EDGE,{"disambiguationData":[TD([[makeQuery(id+"F0.imprint","INTERSECT",VERTEX,{"derivedFrom":[subQ13,subQ0]}),-1.0]])],"derivedFrom":subQ0})])],"isStart":false})])]}),makeQuery(id+"F5.opExtrude","SWEPT_FACE",FACE,{"disambiguationData":[OSD([subQ0]),TDD([makeQuery(id+"F1.opExtrude","CAP_EDGE",EDGE,{"disambiguationData":[OSD([subQ0]),TDD([makeQuery(id+"F0.imprint","IMPRINT",EDGE,{"disambiguationData":[TD([[makeQuery(id+"F0.imprint","INTERSECT",VERTEX,{"derivedFrom":[subQ11,subQ0]}),-1.0]])],"derivedFrom":subQ0})])],"isStart":false})])]}),makeQuery(id+"F5.opExtrude","SWEPT_FACE",FACE,{"disambiguationData":[OSD([subQ0]),TDD([makeQuery(id+"F1.opExtrude","CAP_EDGE",EDGE,{"disambiguationData":[OSD([subQ0]),TDD([makeQuery(id+"F0.imprint","IMPRINT",EDGE,{"disambiguationData":[TD([[makeQuery(id+"F0.imprint","INTERSECT",VERTEX,{"derivedFrom":[subQ9,subQ0]}),-1.0]])],"derivedFrom":subQ0})])],"isStart":false})])]}),makeQuery(id+"F5.opExtrude","SWEPT_FACE",FACE,{"disambiguationData":[OSD([subQ0]),TDD([makeQuery(id+"F1.opExtrude","CAP_EDGE",EDGE,{"disambiguationData":[OSD([subQ0]),TDD([makeQuery(id+"F0.imprint","IMPRINT",EDGE,{"disambiguationData":[TD([[makeQuery(id+"F0.imprint","INTERSECT",VERTEX,{"derivedFrom":[subQ7,subQ0]}),-1.0]])],"derivedFrom":subQ0})])],"isStart":false})])]}),makeQuery(id+"F5.opExtrude","SWEPT_FACE",FACE,{"disambiguationData":[OSD([subQ0]),TDD([makeQuery(id+"F1.opExtrude","CAP_EDGE",EDGE,{"disambiguationData":[OSD([subQ0]),TDD([makeQuery(id+"F0.imprint","IMPRINT",EDGE,{"disambiguationData":[TD([[makeQuery(id+"F0.imprint","INTERSECT",VERTEX,{"derivedFrom":[subQ5,subQ0]}),-1.0]])],"derivedFrom":subQ0})])],"isStart":false})])]}),makeQuery(id+"F5.opExtrude","SWEPT_FACE",FACE,{"disambiguationData":[OSD([subQ0]),TDD([makeQuery(id+"F1.opExtrude","CAP_EDGE",EDGE,{"disambiguationData":[OSD([subQ0]),TDD([makeQuery(id+"F0.imprint","IMPRINT",EDGE,{"disambiguationData":[TD([[makeQuery(id+"F0.imprint","INTERSECT",VERTEX,{"derivedFrom":[subQ3,subQ0]}),-1.0]])],"derivedFrom":subQ0})])],"isStart":false})])]}),makeQuery(id+"F5.opExtrude","SWEPT_FACE",FACE,{"disambiguationData":[OSD([subQ0]),TDD([makeQuery(id+"F1.opExtrude","CAP_EDGE",EDGE,{"disambiguationData":[OSD([subQ0]),TDD([makeQuery(id+"F0.imprint","IMPRINT",EDGE,{"disambiguationData":[TD([[makeQuery(id+"F0.imprint","INTERSECT",VERTEX,{"derivedFrom":[subQ1,subQ0]}),-1.0]])],"derivedFrom":subQ0})])],"isStart":false})])]})]});}
            extrude(context, id + "F9", {"entities" : qUnion([Q0]), "operationType" : NewBodyOperationType.ADD, "endBound" : BoundingType.UP_TO_SURFACE, "endBoundEntityFace" : qUnion([Q1]), "depth" : 25.4 * mm});
        }
        {
            var Q0;
            Q0=makeQuery(id+"F1.opExtrude","SWEPT_FACE",FACE,{"disambiguationData":[OSD([sQuery(id+"F0.wireOp",EDGE,"E1")])]});
            var sketch = newSketch(context, id + "F10", { "sketchPlane" : qUnion([Q0])});
            skPoint(sketch, "E37", {"position": v(82.43, 4.76) * mm});
            skPoint(sketch, "E38", {"position": v(101.48, 4.76) * mm});
            skLineSegment(sketch, "E39", {"start": v(91.95, 9.53) * mm, "end": v(91.95, 0) * mm, "construction": true});
            skSolve(sketch);
        }
        {
            var Q0;
            Q0=sQuery(id+"F10.wireOp",VERTEX,"E37");
            var Q1;
            Q1=sQuery(id+"F10.wireOp",VERTEX,"E38");
            var Q2;
            Q2=makeQuery(id+"F1.opExtrude","SWEPT_BODY",BODY,{"disambiguationData":[OSD([sQuery(id+"F0.wireOp",EDGE,"E0"),sQuery(id+"F0.wireOp",EDGE,"E1"),sQuery(id+"F0.wireOp",EDGE,"E2"),sQuery(id+"F0.wireOp",EDGE,"E3"),sQuery(id+"F0.wireOp",EDGE,"E4"),sQuery(id+"F0.wireOp",EDGE,"E5.1.0.0"),sQuery(id+"F0.wireOp",EDGE,"E5.2.0.0"),sQuery(id+"F0.wireOp",EDGE,"E6.0.3.0"),sQuery(id+"F0.wireOp",EDGE,"E6.0.4.0"),sQuery(id+"F0.wireOp",EDGE,"E6.0.5.0"),sQuery(id+"F0.wireOp",EDGE,"E6.0.6.0"),sQuery(id+"F0.wireOp",EDGE,"E6.0.7.0"),sQuery(id+"F0.wireOp",EDGE,"E7"),sQuery(id+"F0.wireOp",EDGE,"E8.1.0.0"),sQuery(id+"F0.wireOp",EDGE,"E8.2.0.0"),sQuery(id+"F0.wireOp",EDGE,"E9.0.3.0"),sQuery(id+"F0.wireOp",EDGE,"E9.0.4.0"),sQuery(id+"F0.wireOp",EDGE,"E9.0.5.0"),sQuery(id+"F0.wireOp",EDGE,"E9.0.6.0"),sQuery(id+"F0.wireOp",EDGE,"E9.0.7.0"),sQuery(id+"F0.wireOp",EDGE,"E10"),sQuery(id+"F0.wireOp",EDGE,"E11"),sQuery(id+"F0.wireOp",EDGE,"E12"),sQuery(id+"F0.wireOp",EDGE,"E13")])]});
            hole(context, id + "F11", {"style" : HoleStyle.SIMPLE, "endStyle" : HoleEndStyle.BLIND, "standardTappedOrClearance" : lookupTablePath({ "standard" : "ANSI", "engagement" : "75%", "pitch" : "32 tpi", "size" : "#6", "type" : "Tapped" }), "standardBlindInLast" : lookupTablePath({ "standard" : "ANSI", "engagement" : "75%", "pitch" : "32 tpi", "size" : "#6", "type" : "Tapped" }), "holeDiameter" : 2.7 * mm, "holeDepth" : 9.52 * mm, "locations" : qUnion([Q0, Q1]), "scope" : qUnion([Q2]), "tappedDepth" : 12.7 * mm, "tapClearance" : 3, "majorDiameter" : 3.5 * mm});
        }
        {
            var Q0;
            Q0=qCreatedBy(makeId("Front.planeOp"),FACE);
            var sketch = newSketch(context, id + "F12", { "sketchPlane" : qUnion([Q0])});
            skLineSegment(sketch, "E40.0", {"start": v(38.72, -40.2) * mm, "end": v(51.36, -24.3) * mm});
            skLineSegment(sketch, "E41", {"start": v(36.23, -38.23) * mm, "end": v(41.2, -42.18) * mm, "construction": true});
            skLineSegment(sketch, "E42", {"start": v(51.36, -24.3) * mm, "end": v(51.36, -9.52) * mm});
            skLineSegment(sketch, "E43", {"start": v(51.36, -9.52) * mm, "end": v(49.6, -9.52) * mm});
            skArc(sketch, "E44.0", {"start": v(48.22, -28.24) * mm, "mid": v(49.24, -26.38) * mm, "end": v(49.6, -24.3) * mm});
            skLineSegment(sketch, "E44.1", {"start": v(49.6, -9.52) * mm, "end": v(49.6, -24.3) * mm});
            skLineSegment(sketch, "E45", {"start": v(38.72, -40.2) * mm, "end": v(104.44, -149.74) * mm, "construction": true});
            skLineSegment(sketch, "E46", {"start": v(32.14, -12.7) * mm, "end": v(54.53, -12.7) * mm, "construction": true});
            skLineSegment(sketch, "E47.1.0.0", {"start": v(73.75, -24.3) * mm, "end": v(73.75, -9.52) * mm});
            skLineSegment(sketch, "E47.1.0.1", {"start": v(73.75, -9.52) * mm, "end": v(72, -9.52) * mm});
            skLineSegment(sketch, "E47.1.0.2", {"start": v(72, -9.52) * mm, "end": v(72, -24.3) * mm});
            skArc(sketch, "E47.1.0.3", {"start": v(70.62, -28.24) * mm, "mid": v(71.64, -26.38) * mm, "end": v(72, -24.3) * mm});
            skLineSegment(sketch, "E47.2.0.0", {"start": v(96.15, -24.3) * mm, "end": v(96.15, -9.52) * mm});
            skLineSegment(sketch, "E47.2.0.1", {"start": v(96.15, -9.52) * mm, "end": v(94.4, -9.52) * mm});
            skLineSegment(sketch, "E47.2.0.2", {"start": v(94.4, -9.52) * mm, "end": v(94.4, -24.3) * mm});
            skArc(sketch, "E47.2.0.3", {"start": v(93.01, -28.24) * mm, "mid": v(94.04, -26.38) * mm, "end": v(94.4, -24.3) * mm});
            skLineSegment(sketch, "E47.3.0.0", {"start": v(118.55, -24.3) * mm, "end": v(118.55, -9.52) * mm});
            skLineSegment(sketch, "E47.3.0.1", {"start": v(118.55, -9.52) * mm, "end": v(116.79, -9.52) * mm});
            skLineSegment(sketch, "E47.3.0.2", {"start": v(116.79, -9.52) * mm, "end": v(116.79, -24.3) * mm});
            skArc(sketch, "E47.3.0.3", {"start": v(115.41, -28.24) * mm, "mid": v(116.43, -26.38) * mm, "end": v(116.79, -24.3) * mm});
            skLineSegment(sketch, "E47.4.0.0", {"start": v(140.94, -24.3) * mm, "end": v(140.94, -9.52) * mm});
            skLineSegment(sketch, "E47.4.0.1", {"start": v(140.94, -9.52) * mm, "end": v(139.19, -9.52) * mm});
            skLineSegment(sketch, "E47.4.0.2", {"start": v(139.19, -9.52) * mm, "end": v(139.19, -24.3) * mm});
            skArc(sketch, "E47.4.0.3", {"start": v(137.8, -28.24) * mm, "mid": v(138.83, -26.38) * mm, "end": v(139.19, -24.3) * mm});
            skLineSegment(sketch, "E47.5.0.0", {"start": v(163.34, -24.3) * mm, "end": v(163.34, -9.52) * mm});
            skLineSegment(sketch, "E47.5.0.1", {"start": v(163.34, -9.52) * mm, "end": v(161.58, -9.52) * mm});
            skLineSegment(sketch, "E47.5.0.2", {"start": v(161.58, -9.52) * mm, "end": v(161.58, -24.3) * mm});
            skArc(sketch, "E47.5.0.3", {"start": v(160.2, -28.24) * mm, "mid": v(161.23, -26.38) * mm, "end": v(161.58, -24.3) * mm});
            skLineSegment(sketch, "E47.6.0.0", {"start": v(185.74, -24.3) * mm, "end": v(185.74, -9.52) * mm});
            skLineSegment(sketch, "E47.6.0.1", {"start": v(185.74, -9.52) * mm, "end": v(183.98, -9.52) * mm});
            skLineSegment(sketch, "E47.6.0.2", {"start": v(183.98, -9.52) * mm, "end": v(183.98, -24.3) * mm});
            skArc(sketch, "E47.6.0.3", {"start": v(182.6, -28.24) * mm, "mid": v(183.62, -26.38) * mm, "end": v(183.98, -24.3) * mm});
            skLineSegment(sketch, "E47.direction1", {"start": v(43.25, -24.3) * mm, "end": v(65.65, -24.3) * mm, "construction": true});
            skLineSegment(sketch, "E48", {"start": v(73.75, -24.3) * mm, "end": v(48.36, -56.27) * mm});
            skLineSegment(sketch, "E49", {"start": v(96.15, -24.3) * mm, "end": v(58, -72.33) * mm});
            skLineSegment(sketch, "E50", {"start": v(118.55, -24.3) * mm, "end": v(67.63, -88.4) * mm});
            skLineSegment(sketch, "E51", {"start": v(140.94, -24.3) * mm, "end": v(77.27, -104.46) * mm});
            skLineSegment(sketch, "E52", {"start": v(163.34, -24.3) * mm, "end": v(86.91, -120.52) * mm});
            skLineSegment(sketch, "E53", {"start": v(185.74, -24.3) * mm, "end": v(96.55, -136.59) * mm});
            skLineSegment(sketch, "E54", {"start": v(45.87, -54.3) * mm, "end": v(50.84, -58.24) * mm, "construction": true});
            skPoint(sketch, "E55", {"position": v(105.9, -40.2) * mm});
            skLineSegment(sketch, "E56", {"start": v(0, 0) * mm, "end": v(8.1, 0) * mm});
            skLineSegment(sketch, "E57", {"start": v(49.6, -9.52) * mm, "end": v(49.6, 9.53) * mm});
            skLineSegment(sketch, "E58.1.0.0", {"start": v(72, -9.52) * mm, "end": v(72, 9.53) * mm});
            skLineSegment(sketch, "E58.2.0.0", {"start": v(94.4, -9.52) * mm, "end": v(94.4, 9.53) * mm});
            skLineSegment(sketch, "E58.3.0.0", {"start": v(116.79, -9.52) * mm, "end": v(116.79, 9.53) * mm});
            skLineSegment(sketch, "E58.4.0.0", {"start": v(139.19, -9.52) * mm, "end": v(139.19, 9.53) * mm});
            skLineSegment(sketch, "E58.5.0.0", {"start": v(161.58, -9.52) * mm, "end": v(161.58, 9.53) * mm});
            skLineSegment(sketch, "E58.6.0.0", {"start": v(183.98, -9.52) * mm, "end": v(183.98, 9.53) * mm});
            skLineSegment(sketch, "E58.direction1", {"start": v(49.6, -9.52) * mm, "end": v(72, -9.52) * mm, "construction": true});
            skSolve(sketch);
        }
        {
            var Q0;
            Q0=qCreatedBy(makeId("Front.planeOp"),FACE);
            var sketch = newSketch(context, id + "F13", { "sketchPlane" : qUnion([Q0])});
            skLineSegment(sketch, "E59.0", {"start": v(28.96, -23.94) * mm, "end": v(28.96, -9.52) * mm});
            skCircle(sketch, "E59.1", {"center": v(28.96, -23.94) * mm, "radius": 3.18 * mm, "construction": true});
            skLineSegment(sketch, "E59.2", {"start": v(28.96, -23.94) * mm, "end": v(21.69, -11.82) * mm});
            skCircle(sketch, "E59.3", {"center": v(21.69, -11.82) * mm, "radius": 3.18 * mm, "construction": true});
            skLineSegment(sketch, "E60", {"start": v(21.69, -11.82) * mm, "end": v(21.69, 3.17) * mm});
            skLineSegment(sketch, "E61", {"start": v(21.69, 3.17) * mm, "end": v(-3.18, 3.17) * mm});
            skLineSegment(sketch, "E62", {"start": v(28.96, -9.52) * mm, "end": v(206.38, -9.52) * mm});
            skLineSegment(sketch, "E63", {"start": v(0, 0) * mm, "end": v(0, 3.17) * mm});
            skLineSegment(sketch, "E64", {"start": v(206.38, -9.52) * mm, "end": v(241.3, -9.52) * mm});
            skLineSegment(sketch, "E65", {"start": v(-3.18, 3.17) * mm, "end": v(-17.5, 3.17) * mm});
            skSolve(sketch);
        }
        {
            var Q0;
            Q0=makeQuery(id+"F4.opExtrude","CAP_FACE",FACE,{"disambiguationData":[OSD([sQuery(id+"F0.wireOp",EDGE,"E13")])],"isStart":false});
            var sketch = newSketch(context, id + "F14", { "sketchPlane" : qUnion([Q0])});
            skPoint(sketch, "E66", {"position": v(9.26, -4.76) * mm});
            skPoint(sketch, "E66.positionSnap0", {"position": v(0, -4.76) * mm});
            skPoint(sketch, "E66.positionSnap1", {"position": v(9.26, 0) * mm});
            skPoint(sketch, "E67", {"position": v(39.28, -4.76) * mm});
            skPoint(sketch, "E68.1.0.0", {"position": v(61.68, -4.76) * mm});
            skPoint(sketch, "E68.2.0.0", {"position": v(84.07, -4.76) * mm});
            skLineSegment(sketch, "E68.direction1", {"start": v(39.28, -4.76) * mm, "end": v(61.68, -4.76) * mm, "construction": true});
            skPoint(sketch, "E69.0.3.0", {"position": v(106.47, -4.76) * mm});
            skPoint(sketch, "E69.0.4.0", {"position": v(128.87, -4.76) * mm});
            skPoint(sketch, "E69.0.5.0", {"position": v(151.26, -4.76) * mm});
            skPoint(sketch, "E69.0.6.0", {"position": v(173.66, -4.76) * mm});
            skPoint(sketch, "E69.0.7.0", {"position": v(196.06, -4.76) * mm});
            skSolve(sketch);
        }
        {
            var Q0;
            Q0=qCreatedBy(makeId("Front.planeOp"),FACE);
            var sketch = newSketch(context, id + "F15", { "sketchPlane" : qUnion([Q0])});
            skLineSegment(sketch, "E70.bottom", {"start": v(50.8, -38.1) * mm, "end": v(152.4, -38.1) * mm});
            skLineSegment(sketch, "E70.top", {"start": v(50.8, -139.7) * mm, "end": v(152.4, -139.7) * mm});
            skLineSegment(sketch, "E70.left", {"start": v(50.8, -38.1) * mm, "end": v(50.8, -139.7) * mm});
            skLineSegment(sketch, "E70.right", {"start": v(152.4, -38.1) * mm, "end": v(152.4, -139.7) * mm});
            skArc(sketch, "E71.0", {"start": v(70.12, -90.37) * mm, "mid": v(67.43, -91.57) * mm, "end": v(64.91, -90.03) * mm});
            skArc(sketch, "E72.0", {"start": v(79.76, -106.44) * mm, "mid": v(77.06, -107.63) * mm, "end": v(74.55, -106.1) * mm});
            skArc(sketch, "E73.0", {"start": v(41.2, -42.18) * mm, "mid": v(38.51, -43.37) * mm, "end": v(36, -41.84) * mm});
            skArc(sketch, "E73.1", {"start": v(50.84, -58.24) * mm, "mid": v(48.15, -59.44) * mm, "end": v(45.64, -57.9) * mm});
            skArc(sketch, "E74.0", {"start": v(60.48, -74.3) * mm, "mid": v(57.79, -75.5) * mm, "end": v(55.27, -73.97) * mm});
            skCircle(sketch, "E75", {"center": v(38.72, -40.2) * mm, "radius": 2.49 * mm});
            skCircle(sketch, "E76", {"center": v(48.36, -56.27) * mm, "radius": 2.49 * mm});
            skLineSegment(sketch, "E77", {"start": v(101.6, -38.1) * mm, "end": v(101.6, -139.7) * mm, "construction": true});
            skPoint(sketch, "E78.MirrorP", {"position": v(145.2, -72.33) * mm});
            skPoint(sketch, "E79.MirrorP", {"position": v(135.57, -88.4) * mm});
            skLineSegment(sketch, "E80", {"start": v(87.92, -57.76) * mm, "end": v(92.89, -61.7) * mm, "construction": true});
            skLineSegment(sketch, "E81", {"start": v(90.4, -59.73) * mm, "end": v(101.6, -59.73) * mm, "construction": true});
            skLineSegment(sketch, "E82.MirrorCS", {"start": v(112.8, -59.73) * mm, "end": v(101.6, -59.73) * mm, "construction": true});
            skLineSegment(sketch, "E83", {"start": v(110.31, -57.76) * mm, "end": v(115.28, -61.7) * mm, "construction": true});
            skLineSegment(sketch, "E84", {"start": v(87.92, -114.15) * mm, "end": v(92.89, -118.1) * mm, "construction": true});
            skLineSegment(sketch, "E85", {"start": v(90.4, -116.13) * mm, "end": v(101.6, -116.13) * mm, "construction": true});
            skLineSegment(sketch, "E86.MirrorCS", {"start": v(112.8, -116.13) * mm, "end": v(101.6, -116.13) * mm, "construction": true});
            skLineSegment(sketch, "E87", {"start": v(110.31, -114.15) * mm, "end": v(115.28, -118.1) * mm, "construction": true});
            skLineSegment(sketch, "E88", {"start": v(90.4, -59.73) * mm, "end": v(68, -59.73) * mm, "construction": true});
            skLineSegment(sketch, "E89", {"start": v(65.52, -57.76) * mm, "end": v(70.5, -61.7) * mm, "construction": true});
            skLineSegment(sketch, "E90.MirrorCS", {"start": v(112.8, -59.73) * mm, "end": v(135.2, -59.73) * mm, "construction": true});
            skLineSegment(sketch, "E91", {"start": v(132.7, -57.76) * mm, "end": v(137.68, -61.7) * mm, "construction": true});
            skLineSegment(sketch, "E92", {"start": v(74.79, -46.09) * mm, "end": v(79.76, -50.04) * mm, "construction": true});
            skLineSegment(sketch, "E93", {"start": v(77.27, -48.06) * mm, "end": v(77.27, -38.1) * mm, "construction": true});
            skPoint(sketch, "E94.MirrorP", {"position": v(125.93, -48.06) * mm});
            skLineSegment(sketch, "E95", {"start": v(125.96, -94.45) * mm, "end": v(130.93, -98.4) * mm, "construction": true});
            skLineSegment(sketch, "E96", {"start": v(128.44, -96.43) * mm, "end": v(101.6, -96.43) * mm, "construction": true});
            skLineSegment(sketch, "E97.MirrorCS", {"start": v(74.76, -96.43) * mm, "end": v(101.6, -96.43) * mm, "construction": true});
            skLineSegment(sketch, "E98", {"start": v(77.27, -104.46) * mm, "end": v(77.27, -96.43) * mm, "construction": true});
            skLineSegment(sketch, "E99", {"start": v(128.44, -96.43) * mm, "end": v(128.44, -88.4) * mm, "construction": true});
            skLineSegment(sketch, "E100", {"start": v(110.31, -85.96) * mm, "end": v(115.28, -89.9) * mm, "construction": true});
            skLineSegment(sketch, "E101", {"start": v(112.8, -87.93) * mm, "end": v(101.6, -87.93) * mm, "construction": true});
            skLineSegment(sketch, "E102.MirrorCS", {"start": v(90.4, -87.93) * mm, "end": v(101.6, -87.93) * mm, "construction": true});
            skLineSegment(sketch, "E103", {"start": v(87.92, -85.96) * mm, "end": v(92.89, -89.9) * mm, "construction": true});
            skPoint(sketch, "E104", {"position": v(57.15, -120.65) * mm});
            skPoint(sketch, "E105", {"position": v(76.2, -133.35) * mm});
            skPoint(sketch, "E106.MirrorP", {"position": v(146.05, -120.65) * mm});
            skPoint(sketch, "E107.MirrorP", {"position": v(127, -133.35) * mm});
            skSolve(sketch);
        }
        {
            var Q0;
            {var subQ4=sQuery(id+"F15.wireOp",EDGE,"E70.bottom");Q0=makeQuery(id+"F15.imprint","IMPRINT",FACE,{"disambiguationData":[TD([[makeQuery(id+"F15.imprint","IMPRINT",EDGE,{"derivedFrom":subQ4}),-1.0]])]});}
            var Q1;
            {var subQ0=sQuery(id+"F15.wireOp",EDGE,"E76");var subQ4=makeQuery(id+"F15.imprint","IMPRINT",VERTEX,{"disambiguationData":[OD(1.0)],"derivedFrom":subQ0});Q1=makeQuery(id+"F15.imprint","IMPRINT",FACE,{"disambiguationData":[TD([[makeQuery(id+"F15.imprint","IMPRINT",EDGE,{"disambiguationData":[TD([[subQ4,1.0]])],"derivedFrom":subQ0}),1.0]])]});}
            extrude(context, id + "F16", {"entities" : qUnion([Q0, Q1]), "oppositeDirection" : true, "depth" : 6.35 * mm});
        }
        {
            var Q0;
            Q0=sQuery(id+"F15.wireOp",VERTEX,"E74.0.center");
            var Q1;
            Q1=sQuery(id+"F15.wireOp",VERTEX,"E71.0.center");
            var Q2;
            Q2=makeQuery(id+"F16.opExtrude","SWEPT_BODY",BODY,{"disambiguationData":[OSD([sQuery(id+"F15.wireOp",EDGE,"E70.bottom"),sQuery(id+"F15.wireOp",EDGE,"E70.top"),sQuery(id+"F15.wireOp",EDGE,"E70.left"),sQuery(id+"F15.wireOp",EDGE,"E70.right")])]});
            hole(context, id + "F17", {"style" : HoleStyle.SIMPLE, "endStyle" : HoleEndStyle.THROUGH, "standardTappedOrClearance" : lookupTablePath({ "standard" : "ANSI", "engagement" : "75%", "pitch" : "32 tpi", "size" : "#10", "type" : "Tapped" }), "standardBlindInLast" : lookupTablePath({ "standard" : "ANSI", "engagement" : "75%", "pitch" : "32 tpi", "size" : "#10", "type" : "Tapped" }), "holeDiameter" : 4.04 * mm, "showTappedDepth" : true, "isTappedThrough" : true, "tappedDepth" : 6.36 * mm, "tapClearance" : 3, "locations" : qUnion([Q0, Q1]), "scope" : qUnion([Q2]), "majorDiameter" : 4.83 * mm});
        }
        {
            var Q0;
            Q0=sQuery(id+"F15.wireOp",VERTEX,"E72.0.center");
            var Q1;
            Q1=makeQuery(id+"F16.opExtrude","SWEPT_BODY",BODY,{"disambiguationData":[OSD([sQuery(id+"F15.wireOp",EDGE,"E70.bottom"),sQuery(id+"F15.wireOp",EDGE,"E70.top"),sQuery(id+"F15.wireOp",EDGE,"E70.left"),sQuery(id+"F15.wireOp",EDGE,"E70.right")])]});
            hole(context, id + "F18", {"style" : HoleStyle.SIMPLE, "endStyle" : HoleEndStyle.THROUGH, "standardTappedOrClearance" : lookupTablePath({ "standard" : "ANSI", "fit" : "Close", "size" : "#10", "type" : "Clearance" }), "standardBlindInLast" : lookupTablePath({ "fit" : "Close", "standard" : "ANSI", "size" : "#10", "type" : "Clearance" }), "holeDiameter" : 4.98 * mm, "majorDiameter" : 6.35 * mm, "isTappedThrough" : true, "tappedDepth" : 6.38 * mm, "tapClearance" : 3, "locations" : qUnion([Q0]), "scope" : qUnion([Q1])});
        }
        {
            var Q0;
            Q0=makeQuery(id+"F16.opExtrude","CAP_FACE",FACE,{"disambiguationData":[OSD([sQuery(id+"F15.wireOp",EDGE,"E70.bottom"),sQuery(id+"F15.wireOp",EDGE,"E70.top"),sQuery(id+"F15.wireOp",EDGE,"E70.left"),sQuery(id+"F15.wireOp",EDGE,"E70.right"),sQuery(id+"F15.wireOp",EDGE,"E76")])],"isStart":false});
            var sketch = newSketch(context, id + "F19", { "sketchPlane" : qUnion([Q0])});
            skLineSegment(sketch, "E108", {"start": v(-101.6, -38.1) * mm, "end": v(-101.6, -139.7) * mm, "construction": true});
            skSolve(sketch);
        }
        {
            var Q0;
            Q0=qCreatedBy(makeId("Front.planeOp"),FACE);
            var sketch = newSketch(context, id + "F20", { "sketchPlane" : qUnion([Q0])});
            skLineSegment(sketch, "E109.0.0", {"start": v(50.8, -139.7) * mm, "end": v(50.8, -56.75) * mm});
            skLineSegment(sketch, "E109.0.2", {"start": v(50.8, -55.79) * mm, "end": v(50.8, -38.1) * mm});
            skLineSegment(sketch, "E109.0.3", {"start": v(50.8, -38.1) * mm, "end": v(152.4, -38.1) * mm});
            skLineSegment(sketch, "E109.0.4", {"start": v(152.4, -38.1) * mm, "end": v(152.4, -139.7) * mm});
            skLineSegment(sketch, "E109.0.5", {"start": v(152.4, -139.7) * mm, "end": v(50.8, -139.7) * mm});
            skLineSegment(sketch, "E109.1", {"start": v(101.6, -38.1) * mm, "end": v(101.6, -139.7) * mm, "construction": true});
            skLineSegment(sketch, "E110", {"start": v(106.72, -118.68) * mm, "end": v(111.7, -122.62) * mm, "construction": true});
            skLineSegment(sketch, "E111", {"start": v(109.2, -120.65) * mm, "end": v(101.6, -120.65) * mm, "construction": true});
            skLineSegment(sketch, "E112.MirrorCS", {"start": v(94, -120.65) * mm, "end": v(101.6, -120.65) * mm, "construction": true});
            skLineSegment(sketch, "E113", {"start": v(119.03, -131.38) * mm, "end": v(124, -135.32) * mm, "construction": true});
            skLineSegment(sketch, "E114", {"start": v(121.52, -133.35) * mm, "end": v(101.6, -133.35) * mm, "construction": true});
            skLineSegment(sketch, "E115.MirrorCS", {"start": v(81.68, -133.35) * mm, "end": v(101.6, -133.35) * mm, "construction": true});
            skLineSegment(sketch, "E116", {"start": v(101.6, -127) * mm, "end": v(64.88, -127) * mm, "construction": true});
            skLineSegment(sketch, "E117", {"start": v(62.15, -128.63) * mm, "end": v(67.6, -125.37) * mm, "construction": true});
            skLineSegment(sketch, "E118.MirrorCS", {"start": v(101.6, -127) * mm, "end": v(138.32, -127) * mm, "construction": true});
            skLineSegment(sketch, "E119", {"start": v(109.54, -86.93) * mm, "end": v(114.51, -90.87) * mm, "construction": true});
            skLineSegment(sketch, "E120", {"start": v(112.03, -88.9) * mm, "end": v(101.6, -88.9) * mm, "construction": true});
            skLineSegment(sketch, "E121.MirrorCS", {"start": v(91.17, -88.9) * mm, "end": v(101.6, -88.9) * mm, "construction": true});
            skLineSegment(sketch, "E122", {"start": v(101.6, -50.8) * mm, "end": v(142.29, -50.8) * mm, "construction": true});
            skLineSegment(sketch, "E123", {"start": v(117.4, -48.83) * mm, "end": v(122.38, -52.77) * mm, "construction": true});
            skLineSegment(sketch, "E124", {"start": v(139.8, -48.83) * mm, "end": v(144.77, -52.77) * mm, "construction": true});
            skPoint(sketch, "E125", {"position": v(119.9, -50.8) * mm});
            skLineSegment(sketch, "E126.MirrorCS", {"start": v(101.6, -50.8) * mm, "end": v(60.91, -50.8) * mm, "construction": true});
            skLineSegment(sketch, "E127.MirrorCS", {"start": v(63.4, -48.83) * mm, "end": v(58.43, -52.77) * mm, "construction": true});
            skLineSegment(sketch, "E128", {"start": v(101.6, -44.45) * mm, "end": v(57.74, -44.45) * mm, "construction": true});
            skLineSegment(sketch, "E129", {"start": v(55.26, -42.48) * mm, "end": v(60.23, -46.42) * mm, "construction": true});
            skLineSegment(sketch, "E130", {"start": v(77.66, -42.48) * mm, "end": v(82.63, -46.42) * mm, "construction": true});
            skLineSegment(sketch, "E131", {"start": v(89.97, -55.18) * mm, "end": v(94.94, -59.12) * mm, "construction": true});
            skPoint(sketch, "E132", {"position": v(80.14, -44.45) * mm});
            skLineSegment(sketch, "E133", {"start": v(92.45, -57.15) * mm, "end": v(101.6, -57.15) * mm, "construction": true});
            skLineSegment(sketch, "E134.MirrorCS", {"start": v(110.75, -57.15) * mm, "end": v(101.6, -57.15) * mm, "construction": true});
            skPoint(sketch, "E135.MirrorP", {"position": v(123.06, -44.45) * mm});
            skLineSegment(sketch, "E136.MirrorCS", {"start": v(101.6, -44.45) * mm, "end": v(145.46, -44.45) * mm, "construction": true});
            skPoint(sketch, "E137.MirrorP", {"position": v(83.3, -50.8) * mm});
            skLineSegment(sketch, "E138", {"start": v(101.6, -101.6) * mm, "end": v(146.73, -101.6) * mm, "construction": true});
            skLineSegment(sketch, "E139", {"start": v(144.25, -99.63) * mm, "end": v(149.22, -103.57) * mm, "construction": true});
            skLineSegment(sketch, "E140.MirrorCS", {"start": v(101.6, -101.6) * mm, "end": v(56.47, -101.6) * mm, "construction": true});
            skLineSegment(sketch, "E141", {"start": v(101.6, -95.25) * mm, "end": v(129.38, -95.25) * mm, "construction": true});
            skLineSegment(sketch, "E142", {"start": v(126.9, -93.28) * mm, "end": v(131.87, -97.22) * mm, "construction": true});
            skLineSegment(sketch, "E143.MirrorCS", {"start": v(101.6, -95.25) * mm, "end": v(73.82, -95.25) * mm, "construction": true});
            skPoint(sketch, "E144", {"position": v(57.74, -44.45) * mm});
            skPoint(sketch, "E145", {"position": v(145.46, -44.45) * mm});
            skPoint(sketch, "E146", {"position": v(60.91, -50.8) * mm});
            skPoint(sketch, "E147", {"position": v(142.29, -50.8) * mm});
            skPoint(sketch, "E148", {"position": v(110.75, -57.15) * mm});
            skPoint(sketch, "E149", {"position": v(92.45, -57.15) * mm});
            skPoint(sketch, "E150", {"position": v(112.03, -88.9) * mm});
            skPoint(sketch, "E151", {"position": v(91.17, -88.9) * mm});
            skPoint(sketch, "E152", {"position": v(73.82, -95.25) * mm});
            skPoint(sketch, "E153", {"position": v(129.38, -95.25) * mm});
            skPoint(sketch, "E154", {"position": v(146.73, -101.6) * mm});
            skPoint(sketch, "E155", {"position": v(56.47, -101.6) * mm});
            skPoint(sketch, "E156", {"position": v(94, -120.65) * mm});
            skPoint(sketch, "E157", {"position": v(109.2, -120.65) * mm});
            skPoint(sketch, "E158", {"position": v(138.32, -127) * mm});
            skPoint(sketch, "E159", {"position": v(64.88, -127) * mm});
            skPoint(sketch, "E160", {"position": v(81.68, -133.35) * mm});
            skPoint(sketch, "E161", {"position": v(121.52, -133.35) * mm});
            skSolve(sketch);
        }
        {
            var Q0;
            Q0=sQuery(id+"F20.wireOp",VERTEX,"E144");
            var Q1;
            Q1=sQuery(id+"F20.wireOp",VERTEX,"E132");
            var Q2;
            Q2=sQuery(id+"F20.wireOp",VERTEX,"E149");
            var Q3;
            Q3=sQuery(id+"F20.wireOp",VERTEX,"E125");
            var Q4;
            Q4=sQuery(id+"F20.wireOp",VERTEX,"E147");
            var Q5;
            Q5=sQuery(id+"F20.wireOp",VERTEX,"E150");
            var Q6;
            Q6=sQuery(id+"F20.wireOp",VERTEX,"E153");
            var Q7;
            Q7=sQuery(id+"F20.wireOp",VERTEX,"E154");
            var Q8;
            Q8=sQuery(id+"F20.wireOp",VERTEX,"E157");
            var Q9;
            Q9=sQuery(id+"F20.wireOp",VERTEX,"E159");
            var Q10;
            Q10=sQuery(id+"F20.wireOp",VERTEX,"E161");
            var Q11;
            Q11=makeQuery(id+"F16.opExtrude","SWEPT_BODY",BODY,{"disambiguationData":[OSD([sQuery(id+"F15.wireOp",EDGE,"E70.bottom"),sQuery(id+"F15.wireOp",EDGE,"E70.top"),sQuery(id+"F15.wireOp",EDGE,"E70.left"),sQuery(id+"F15.wireOp",EDGE,"E70.right"),sQuery(id+"F15.wireOp",EDGE,"E76")])]});
            hole(context, id + "F21", {"style" : HoleStyle.SIMPLE, "endStyle" : HoleEndStyle.THROUGH, "standardTappedOrClearance" : lookupTablePath({ "standard" : "ANSI", "engagement" : "75%", "pitch" : "32 tpi", "size" : "#10", "type" : "Tapped" }), "standardBlindInLast" : lookupTablePath({ "standard" : "ANSI", "engagement" : "75%", "pitch" : "32 tpi", "size" : "#10", "type" : "Tapped" }), "holeDiameter" : 4.04 * mm, "showTappedDepth" : true, "isTappedThrough" : true, "tappedDepth" : 6.38 * mm, "tapClearance" : 3, "locations" : qUnion([Q0, Q1, Q2, Q3, Q4, Q5, Q6, Q7, Q8, Q9, Q10]), "scope" : qUnion([Q11]), "majorDiameter" : 4.83 * mm});
        }
        {
            var Q0;
            Q0=sQuery(id+"F14.wireOp",VERTEX,"E69.0.7.0");
            var Q1;
            Q1=sQuery(id+"F14.wireOp",VERTEX,"E69.0.6.0");
            var Q2;
            Q2=sQuery(id+"F14.wireOp",VERTEX,"E69.0.5.0");
            var Q3;
            Q3=sQuery(id+"F14.wireOp",VERTEX,"E69.0.4.0");
            var Q4;
            Q4=sQuery(id+"F14.wireOp",VERTEX,"E69.0.3.0");
            var Q5;
            Q5=sQuery(id+"F14.wireOp",VERTEX,"E68.2.0.0");
            var Q6;
            Q6=sQuery(id+"F14.wireOp",VERTEX,"E68.1.0.0");
            var Q7;
            Q7=sQuery(id+"F14.wireOp",VERTEX,"E67");
            var Q8;
            Q8=sQuery(id+"F14.wireOp",VERTEX,"E66");
            var Q9;
            Q9=makeQuery(id+"F1.opExtrude","SWEPT_BODY",BODY,{"disambiguationData":[OSD([sQuery(id+"F0.wireOp",EDGE,"E0"),sQuery(id+"F0.wireOp",EDGE,"E1"),sQuery(id+"F0.wireOp",EDGE,"E2"),sQuery(id+"F0.wireOp",EDGE,"E3"),sQuery(id+"F0.wireOp",EDGE,"E4"),sQuery(id+"F0.wireOp",EDGE,"E5.1.0.0"),sQuery(id+"F0.wireOp",EDGE,"E5.2.0.0"),sQuery(id+"F0.wireOp",EDGE,"E6.0.3.0"),sQuery(id+"F0.wireOp",EDGE,"E6.0.4.0"),sQuery(id+"F0.wireOp",EDGE,"E6.0.5.0"),sQuery(id+"F0.wireOp",EDGE,"E6.0.6.0"),sQuery(id+"F0.wireOp",EDGE,"E6.0.7.0"),sQuery(id+"F0.wireOp",EDGE,"E7"),sQuery(id+"F0.wireOp",EDGE,"E8.1.0.0"),sQuery(id+"F0.wireOp",EDGE,"E8.2.0.0"),sQuery(id+"F0.wireOp",EDGE,"E9.0.3.0"),sQuery(id+"F0.wireOp",EDGE,"E9.0.4.0"),sQuery(id+"F0.wireOp",EDGE,"E9.0.5.0"),sQuery(id+"F0.wireOp",EDGE,"E9.0.6.0"),sQuery(id+"F0.wireOp",EDGE,"E9.0.7.0"),sQuery(id+"F0.wireOp",EDGE,"E10"),sQuery(id+"F0.wireOp",EDGE,"E11"),sQuery(id+"F0.wireOp",EDGE,"E12"),sQuery(id+"F0.wireOp",EDGE,"E13")])]});
            hole(context, id + "F22", {"style" : HoleStyle.SIMPLE, "endStyle" : HoleEndStyle.BLIND, "standardTappedOrClearance" : lookupTablePath({ "standard" : "ANSI", "size" : "19/64 (0.3)", "type" : "Drilled" }), "standardBlindInLast" : lookupTablePath({ "standard" : "ANSI", "size" : "19/64 (0.3)", "type" : "Drilled" }), "holeDiameter" : 19 / 1625.6 * mm, "majorDiameter" : 9.52 * mm, "holeDepth" : 14.29 * mm, "tappedDepth" : 9.53 * mm, "tapClearance" : 3, "locations" : qUnion([Q0, Q1, Q2, Q3, Q4, Q5, Q6, Q7, Q8]), "scope" : qUnion([Q9])});
        }
    });
